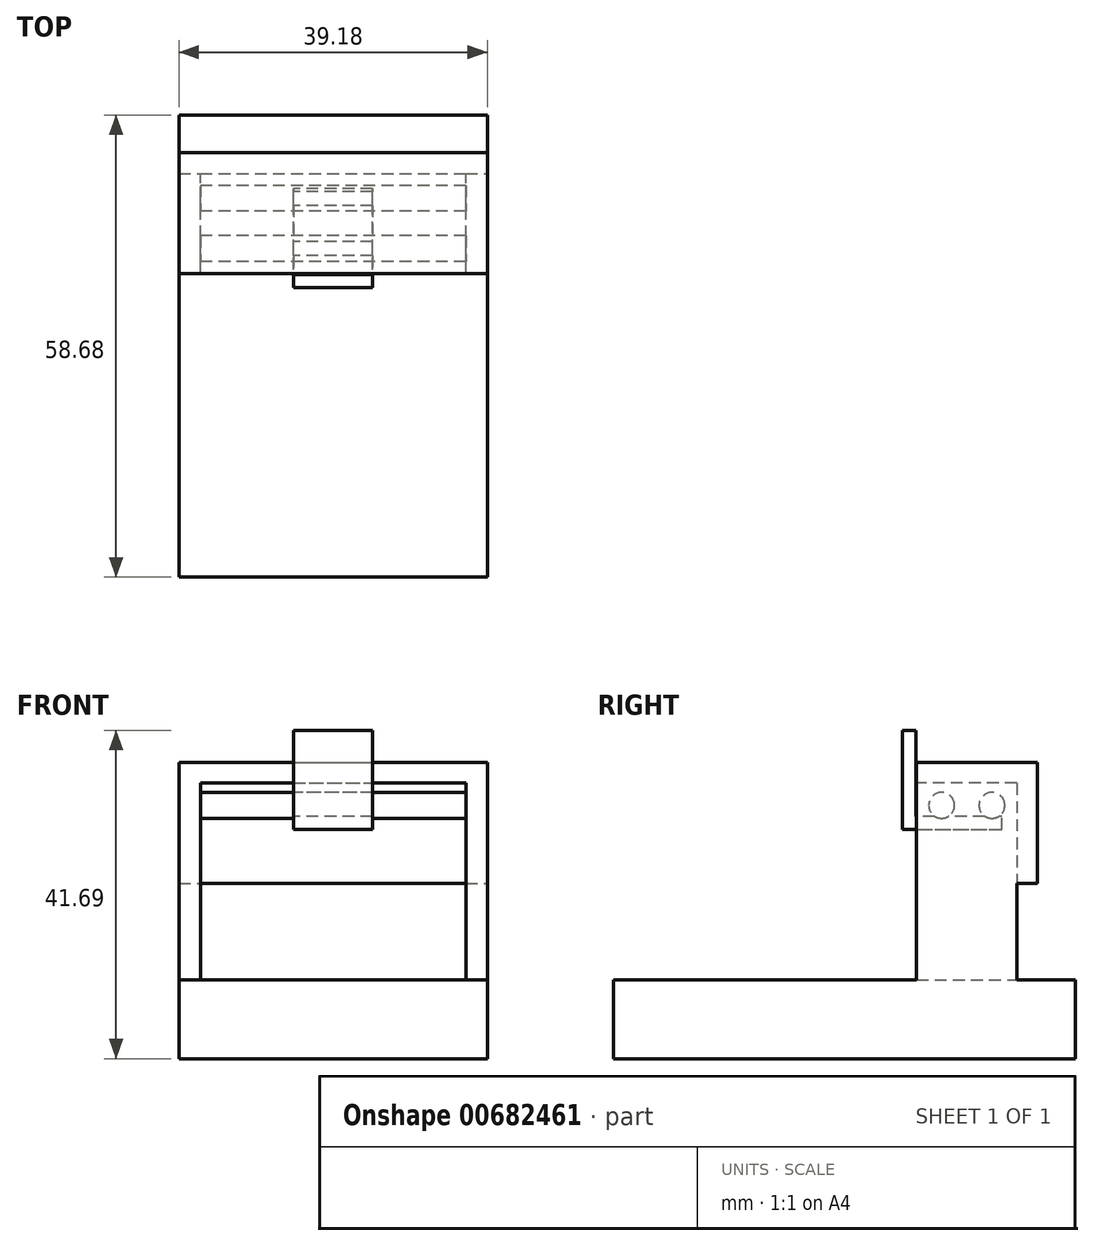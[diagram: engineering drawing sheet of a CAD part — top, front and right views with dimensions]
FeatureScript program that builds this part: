
annotation { "Feature Type Name" : "Feature", "Feature Type Description" : "" }
export const myFeature = defineFeature(function(context is Context, id is Id, definition is map)
    precondition{}
    {
        {
            var Q0;
            Q0=qCreatedBy(makeId("Top.planeOp"),FACE);
            var sketch = newSketch(context, id + "F0", { "sketchPlane" : qUnion([Q0])});
            skLineSegment(sketch, "E0.bottom", {"start": v(-19.59, 29.34) * mm, "end": v(19.59, 29.34) * mm});
            skLineSegment(sketch, "E0.top", {"start": v(-19.59, -29.34) * mm, "end": v(19.59, -29.34) * mm});
            skLineSegment(sketch, "E0.left", {"start": v(-19.59, 29.34) * mm, "end": v(-19.59, -29.34) * mm});
            skLineSegment(sketch, "E0.right", {"start": v(19.59, 29.34) * mm, "end": v(19.59, -29.34) * mm});
            skPoint(sketch, "E0.middle", {"position": v(0, 0) * mm});
            skLineSegment(sketch, "E1.bottom", {"start": v(-19.59, 21.92) * mm, "end": v(-16.85, 21.92) * mm});
            skLineSegment(sketch, "E1.top", {"start": v(-19.59, 9.19) * mm, "end": v(-16.85, 9.19) * mm});
            skLineSegment(sketch, "E1.left", {"start": v(-19.59, 21.92) * mm, "end": v(-19.59, 9.19) * mm});
            skLineSegment(sketch, "E1.right", {"start": v(-16.85, 21.92) * mm, "end": v(-16.85, 9.19) * mm});
            skLineSegment(sketch, "E2.MirrorCS", {"start": v(19.59, 21.92) * mm, "end": v(16.85, 21.92) * mm});
            skLineSegment(sketch, "E3.MirrorCS", {"start": v(19.59, 9.19) * mm, "end": v(16.85, 9.19) * mm});
            skLineSegment(sketch, "E4.MirrorCS", {"start": v(19.59, 21.92) * mm, "end": v(19.59, 9.19) * mm});
            skLineSegment(sketch, "E5.MirrorCS", {"start": v(16.85, 21.92) * mm, "end": v(16.85, 9.19) * mm});
            skSolve(sketch);
        }
        {
            var Q0;
            Q0 = qSketchRegion(id + "F0", true);
            extrude(context, id + "F1", {"entities" : qUnion([Q0]), "depth" : 10 * mm, "offsetDistance" : 25 * mm});
        }
        {
            var Q0;
            Q0=makeQuery(id+"F0.imprint","IMPRINT",FACE,{"disambiguationData":[TD([[makeQuery(id+"F0.imprint","IMPRINT",EDGE,{"derivedFrom":sQuery(id+"F0.wireOp",EDGE,"E1.bottom")}),-1.0]])]});
            var Q1;
            Q1=makeQuery(id+"F0.imprint","IMPRINT",FACE,{"disambiguationData":[TD([[makeQuery(id+"F0.imprint","IMPRINT",EDGE,{"derivedFrom":sQuery(id+"F0.wireOp",EDGE,"E2.MirrorCS")}),1.0]])]});
            extrude(context, id + "F2", {"entities" : qUnion([Q0, Q1]), "operationType" : NewBodyOperationType.ADD, "depth" : 35 * mm, "offsetDistance" : 25 * mm});
        }
        {
            var Q0;
            Q0=makeQuery(id+"F2.opExtrude","SWEPT_FACE",FACE,{"disambiguationData":[OSD([sQuery(id+"F0.wireOp",EDGE,"E1.right")])]});
            var sketch = newSketch(context, id + "F3", { "sketchPlane" : qUnion([Q0])});
            skCircle(sketch, "E6", {"center": v(12.36, 32.18) * mm, "radius": 1.64 * mm});
            skCircle(sketch, "E7", {"center": v(18.75, 32.18) * mm, "radius": 1.64 * mm});
            skLineSegment(sketch, "E8", {"start": v(12.36, 32.18) * mm, "end": v(18.75, 32.18) * mm, "construction": true});
            skLineSegment(sketch, "E9", {"start": v(12.36, 32.18) * mm, "end": v(9.19, 32.18) * mm, "construction": true});
            skLineSegment(sketch, "E10", {"start": v(18.75, 32.18) * mm, "end": v(21.92, 32.18) * mm, "construction": true});
            skSolve(sketch);
        }
        {
            var Q0;
            Q0 = qSketchRegion(id + "F3", true);
            var Q1;
            Q1=makeQuery(id+"F2.opExtrude","SWEPT_FACE",FACE,{"disambiguationData":[OSD([sQuery(id+"F0.wireOp",EDGE,"E5.MirrorCS")])]});
            extrude(context, id + "F4", {"entities" : qUnion([Q0]), "operationType" : NewBodyOperationType.ADD, "endBound" : BoundingType.UP_TO_SURFACE, "depth" : 25 * mm, "endBoundEntityFace" : qUnion([Q1]), "offsetDistance" : 25 * mm});
        }
        {
            var Q0;
            {var subQ0=sQuery(id+"F0.wireOp",EDGE,"E4.MirrorCS");Q0=makeQuery(id+"F2.boolean.opBoolean","MERGE",FACE,{"derivedFrom":[makeQuery(id+"F1.opExtrude","SWEPT_FACE",FACE,{"disambiguationData":[OSD([sQuery(id+"F0.wireOp",EDGE,"E0.right"),subQ0])]}),makeQuery(id+"F2.opExtrude","SWEPT_FACE",FACE,{"disambiguationData":[OSD([subQ0])]})]});}
            var sketch = newSketch(context, id + "F5", { "sketchPlane" : qUnion([Q0])});
            skLineSegment(sketch, "E11", {"start": v(9.19, 35) * mm, "end": v(9.19, 37.63) * mm});
            skLineSegment(sketch, "E12", {"start": v(9.19, 37.63) * mm, "end": v(24.56, 37.63) * mm});
            skLineSegment(sketch, "E13", {"start": v(24.56, 37.63) * mm, "end": v(24.56, 22.26) * mm});
            skLineSegment(sketch, "E14", {"start": v(24.56, 22.26) * mm, "end": v(21.92, 22.26) * mm});
            skLineSegment(sketch, "E15", {"start": v(21.92, 22.26) * mm, "end": v(21.92, 35) * mm});
            skLineSegment(sketch, "E16", {"start": v(21.92, 35) * mm, "end": v(9.19, 35) * mm});
            skSolve(sketch);
        }
        {
            var Q0;
            Q0 = qSketchRegion(id + "F5", true);
            var Q1;
            {var subQ0=sQuery(id+"F0.wireOp",EDGE,"E1.left");Q1=makeQuery(id+"F2.boolean.opBoolean","MERGE",FACE,{"derivedFrom":[makeQuery(id+"F1.opExtrude","SWEPT_FACE",FACE,{"disambiguationData":[OSD([sQuery(id+"F0.wireOp",EDGE,"E0.left"),subQ0])]}),makeQuery(id+"F2.opExtrude","SWEPT_FACE",FACE,{"disambiguationData":[OSD([subQ0])]})]});}
            extrude(context, id + "F6", {"entities" : qUnion([Q0]), "operationType" : NewBodyOperationType.ADD, "endBound" : BoundingType.UP_TO_SURFACE, "oppositeDirection" : true, "depth" : 25 * mm, "endBoundEntityFace" : qUnion([Q1]), "offsetDistance" : 25 * mm});
        }
        {
            var Q0;
            Q0=qCreatedBy(makeId("Right.planeOp"),FACE);
            var sketch = newSketch(context, id + "F7", { "sketchPlane" : qUnion([Q0])});
            skLineSegment(sketch, "E17", {"start": v(19.99, 30.8) * mm, "end": v(9.1, 30.8) * mm});
            skLineSegment(sketch, "E18", {"start": v(9.1, 30.8) * mm, "end": v(9.1, 41.69) * mm});
            skLineSegment(sketch, "E19", {"start": v(9.1, 41.69) * mm, "end": v(7.41, 41.69) * mm});
            skLineSegment(sketch, "E20", {"start": v(7.41, 41.69) * mm, "end": v(7.41, 29.11) * mm});
            skLineSegment(sketch, "E21", {"start": v(7.41, 29.11) * mm, "end": v(19.99, 29.11) * mm});
            skLineSegment(sketch, "E22", {"start": v(19.99, 29.11) * mm, "end": v(19.99, 30.8) * mm});
            skSolve(sketch);
        }
        {
            var Q0;
            Q0 = qSketchRegion(id + "F7", true);
            extrude(context, id + "F8", {"entities" : qUnion([Q0]), "operationType" : NewBodyOperationType.ADD, "endBound" : BoundingType.SYMMETRIC, "depth" : 10 * mm, "offsetDistance" : 25 * mm});
        }
    });
